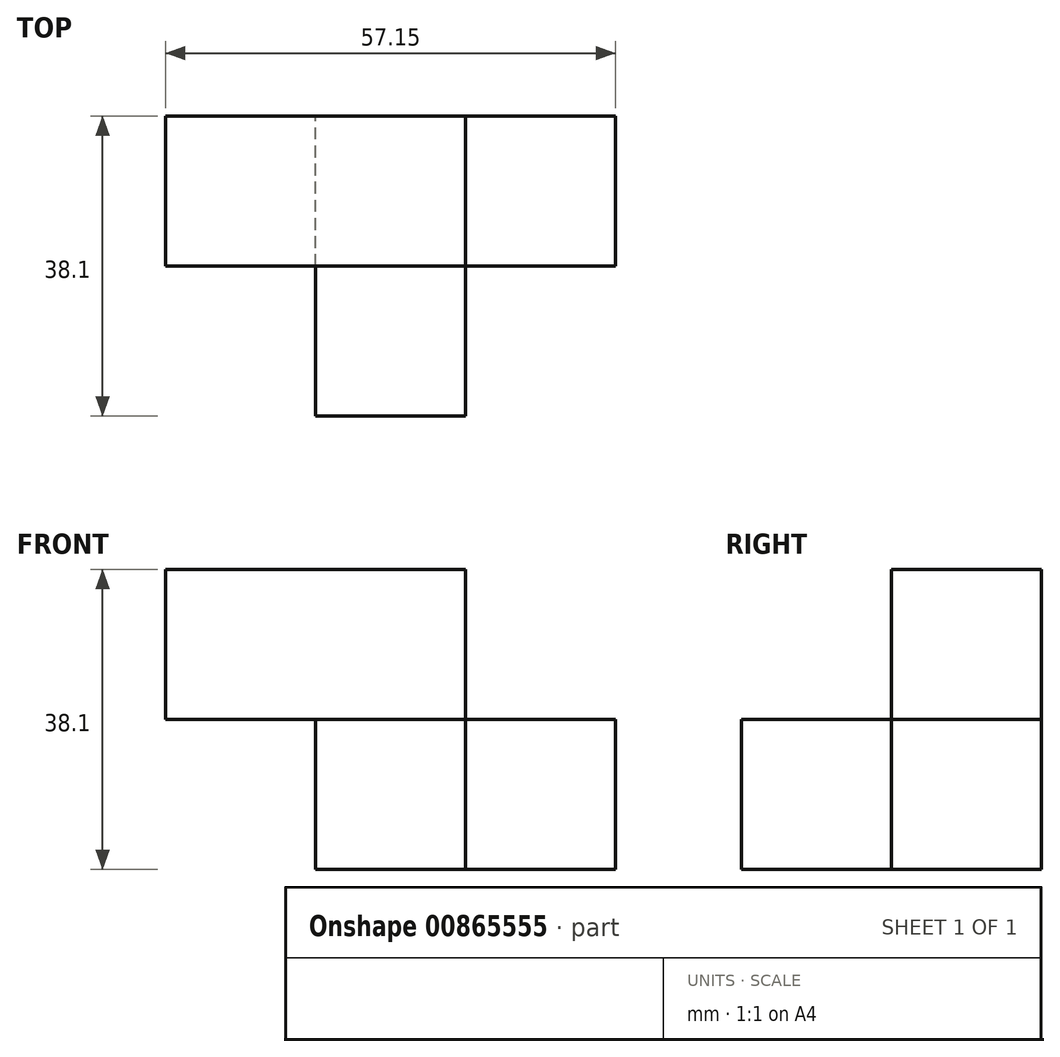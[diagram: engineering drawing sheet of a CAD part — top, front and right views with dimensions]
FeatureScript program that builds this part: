
annotation { "Feature Type Name" : "Feature", "Feature Type Description" : "" }
export const myFeature = defineFeature(function(context is Context, id is Id, definition is map)
    precondition{}
    {
        {
            var Q0;
            Q0=qCreatedBy(makeId("Front.planeOp"),FACE);
            var sketch = newSketch(context, id + "F0", { "sketchPlane" : qUnion([Q0])});
            skLineSegment(sketch, "E0", {"start": v(0, 0) * mm, "end": v(38.1, 0) * mm});
            skLineSegment(sketch, "E1", {"start": v(38.1, 0) * mm, "end": v(38.1, 19.05) * mm});
            skLineSegment(sketch, "E2", {"start": v(38.1, 19.05) * mm, "end": v(19.05, 19.05) * mm});
            skLineSegment(sketch, "E3", {"start": v(19.05, 19.05) * mm, "end": v(19.05, 38.1) * mm});
            skLineSegment(sketch, "E4", {"start": v(19.05, 38.1) * mm, "end": v(-19.05, 38.1) * mm});
            skLineSegment(sketch, "E5", {"start": v(-19.05, 38.1) * mm, "end": v(-19.05, 19.05) * mm});
            skLineSegment(sketch, "E6", {"start": v(-19.05, 19.05) * mm, "end": v(0, 19.05) * mm});
            skLineSegment(sketch, "E7", {"start": v(0, 19.05) * mm, "end": v(0, 0) * mm});
            skSolve(sketch);
        }
        {
            var Q0;
            Q0=makeQuery(id+"F0.imprint","IMPRINT",FACE,{"disambiguationData":[TD([[makeQuery(id+"F0.imprint","IMPRINT",EDGE,{"derivedFrom":sQuery(id+"F0.wireOp",EDGE,"E0")}),1.0]])]});
            extrude(context, id + "F1", {"entities" : qUnion([Q0]), "depth" : 19.05 * mm, "offsetDistance" : 25.4 * mm});
        }
        {
            var Q0;
            Q0=makeQuery(id+"F1.opExtrude","CAP_FACE",FACE,{"disambiguationData":[OSD([sQuery(id+"F0.wireOp",EDGE,"E0"),sQuery(id+"F0.wireOp",EDGE,"E1"),sQuery(id+"F0.wireOp",EDGE,"E2"),sQuery(id+"F0.wireOp",EDGE,"E3"),sQuery(id+"F0.wireOp",EDGE,"E4"),sQuery(id+"F0.wireOp",EDGE,"E5"),sQuery(id+"F0.wireOp",EDGE,"E6"),sQuery(id+"F0.wireOp",EDGE,"E7")])],"isStart":false});
            var sketch = newSketch(context, id + "F2", { "sketchPlane" : qUnion([Q0])});
            skLineSegment(sketch, "E8", {"start": v(0, 19.05) * mm, "end": v(19.05, 19.05) * mm});
            skLineSegment(sketch, "E9", {"start": v(19.05, 19.05) * mm, "end": v(19.05, 0) * mm});
            skSolve(sketch);
        }
        {
            var Q0;
            Q0=makeQuery(id+"F2.imprint","IMPRINT",FACE,{"disambiguationData":[TD([[makeQuery(id+"F2.imprint","IMPRINT",EDGE,{"derivedFrom":sQuery(id+"F2.wireOp",EDGE,"E8")}),-1.0]])]});
            extrude(context, id + "F3", {"entities" : qUnion([Q0]), "operationType" : NewBodyOperationType.ADD, "depth" : 19.05 * mm, "offsetDistance" : 25.4 * mm});
        }
    });
